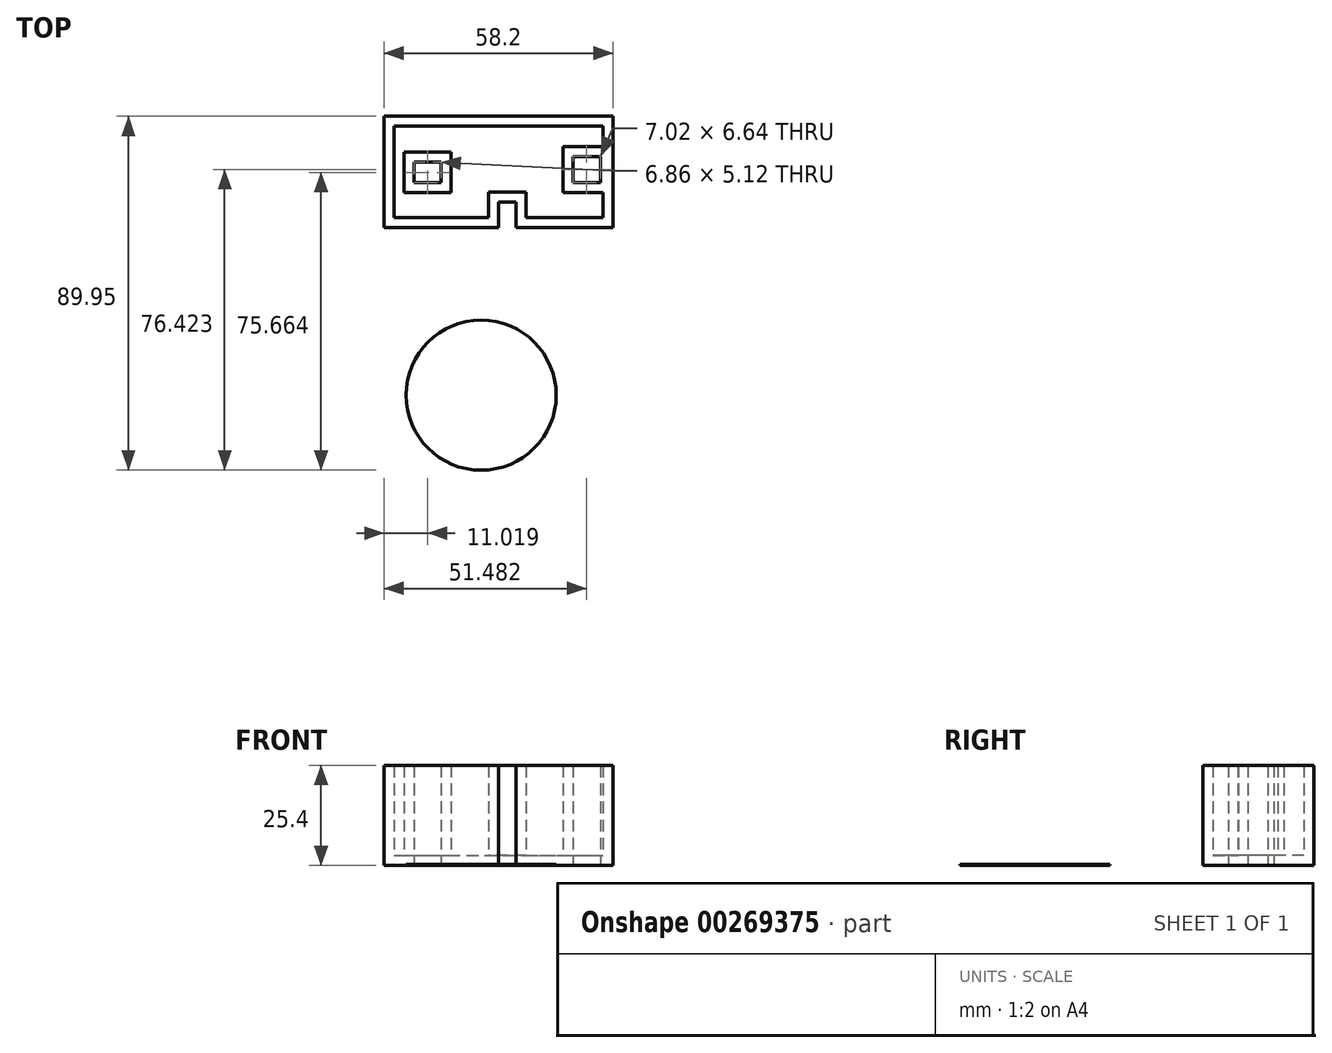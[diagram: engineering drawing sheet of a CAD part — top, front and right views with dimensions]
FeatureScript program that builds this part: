
annotation { "Feature Type Name" : "Feature", "Feature Type Description" : "" }
export const myFeature = defineFeature(function(context is Context, id is Id, definition is map)
    precondition{}
    {
        {
            var Q0;
            Q0=qCreatedBy(makeId("Top.planeOp"),FACE);
            var sketch = newSketch(context, id + "F0", { "sketchPlane" : qUnion([Q0])});
            skLineSegment(sketch, "E0.bottom", {"start": v(11.18, 38.08) * mm, "end": v(69.38, 38.08) * mm});
            skLineSegment(sketch, "E0.top", {"start": v(11.18, 9.83) * mm, "end": v(40.28, 9.83) * mm});
            skLineSegment(sketch, "E0.left", {"start": v(11.18, 38.08) * mm, "end": v(11.18, 9.83) * mm});
            skLineSegment(sketch, "E0.right", {"start": v(69.38, 38.08) * mm, "end": v(69.38, 9.83) * mm});
            skPoint(sketch, "E1.oppositeSnap0", {"position": v(40.28, 9.83) * mm});
            skLineSegment(sketch, "E1.top", {"start": v(44.73, 16.27) * mm, "end": v(40.28, 16.27) * mm});
            skLineSegment(sketch, "E1.left", {"start": v(44.73, 9.83) * mm, "end": v(44.73, 16.27) * mm});
            skLineSegment(sketch, "E1.right", {"start": v(40.28, 9.83) * mm, "end": v(40.28, 16.27) * mm});
            skLineSegment(sketch, "E2.trimOffspring", {"start": v(44.73, 9.83) * mm, "end": v(69.38, 9.83) * mm});
            skLineSegment(sketch, "E3.1", {"start": v(69.38, 38.08) * mm, "end": v(40, 69.4) * mm});
            skLineSegment(sketch, "E3.2", {"start": v(40, 69.4) * mm, "end": v(11.18, 38.08) * mm});
            skText(sketch, "E4", { "text": "SoMy", "fontName": "AllertaStencil-Regular.ttf"});
            skLineSegment(sketch, "E5.bottom", {"start": v(-62, 37.35) * mm, "end": v(-14.22, 37.35) * mm});
            skLineSegment(sketch, "E5.top", {"start": v(-62, 20.48) * mm, "end": v(-14.22, 20.48) * mm});
            skLineSegment(sketch, "E5.left", {"start": v(-62, 37.35) * mm, "end": v(-62, 20.48) * mm});
            skLineSegment(sketch, "E5.right", {"start": v(-14.22, 37.35) * mm, "end": v(-14.22, 20.48) * mm});
            skCircle(sketch, "E6", {"center": v(-37.4, 29.2) * mm, "radius": 9.47 * mm});
            skCircle(sketch, "E7", {"center": v(35.83, -32.8) * mm, "radius": 19.07 * mm});
            skCircle(sketch, "E8", {"center": v(35.83, -32.8) * mm, "radius": 9.53 * mm});
            skCircle(sketch, "E9", {"center": v(35.83, -32.8) * mm, "radius": 14.21 * mm});
            skCircle(sketch, "E10", {"center": v(-44.56, -17.44) * mm, "radius": 10.06 * mm});
            skLineSegment(sketch, "E11.bottom", {"start": v(59.15, 27.87) * mm, "end": v(66.17, 27.87) * mm});
            skLineSegment(sketch, "E11.top", {"start": v(59.15, 21.23) * mm, "end": v(66.17, 21.23) * mm});
            skLineSegment(sketch, "E11.left", {"start": v(59.15, 27.87) * mm, "end": v(59.15, 21.23) * mm});
            skLineSegment(sketch, "E11.right", {"start": v(66.17, 27.87) * mm, "end": v(66.17, 21.23) * mm});
            skLineSegment(sketch, "E12.bottom", {"start": v(18.77, 26.35) * mm, "end": v(25.63, 26.35) * mm});
            skLineSegment(sketch, "E12.top", {"start": v(18.77, 21.23) * mm, "end": v(25.63, 21.23) * mm});
            skLineSegment(sketch, "E12.left", {"start": v(18.77, 26.35) * mm, "end": v(18.77, 21.23) * mm});
            skLineSegment(sketch, "E12.right", {"start": v(25.63, 26.35) * mm, "end": v(25.63, 21.23) * mm});
            const initialGuessF0  = {"E4": [-0.06295, -0.06086, 1, 0, 0.01332]};
            skSetInitialGuess(sketch, initialGuessF0);
            skSolve(sketch);
        }
        {
            var Q0;
            Q0=sQuery(id+"F0.wireOp",EDGE,"E7");
            extrude(context, id + "F1", {"bodyType" : ToolBodyType.SURFACE, "surfaceEntities" : qUnion([Q0]), "oppositeDirection" : true, "depth" : 127.76 * mm});
        }
        {
            var Q0;
            Q0=sQuery(id+"F0.wireOp",EDGE,"E9");
            extrude(context, id + "F2", {"bodyType" : ToolBodyType.SURFACE, "surfaceEntities" : qUnion([Q0]), "depth" : 4.57 * mm});
        }
        {
            var Q0;
            Q0=sQuery(id+"F0.wireOp",EDGE,"E8");
            extrude(context, id + "F3", {"bodyType" : ToolBodyType.SURFACE, "surfaceEntities" : qUnion([Q0]), "depth" : 9.14 * mm});
        }
        {
            var Q0;
            Q0=makeQuery(id+"F0.imprint","IMPRINT",FACE,{"disambiguationData":[TD([[makeQuery(id+"F0.imprint","IMPRINT",EDGE,{"derivedFrom":sQuery(id+"F0.wireOp",EDGE,"E7")}),1.0]])]});
            var Q1;
            Q1=makeQuery(id+"F0.imprint","IMPRINT",FACE,{"disambiguationData":[TD([[makeQuery(id+"F0.imprint","IMPRINT",EDGE,{"derivedFrom":sQuery(id+"F0.wireOp",EDGE,"E8")}),-1.0]])]});
            var Q2;
            Q2=makeQuery(id+"F0.imprint","IMPRINT",FACE,{"disambiguationData":[TD([[makeQuery(id+"F0.imprint","IMPRINT",EDGE,{"derivedFrom":sQuery(id+"F0.wireOp",EDGE,"E8")}),1.0]])]});
            extrude(context, id + "F4", {"entities" : qUnion([Q0, Q1, Q2]), "depth" : 0.25 * mm});
        }
        {
            var Q0;
            Q0=makeQuery(id+"F0.imprint","IMPRINT",FACE,{"disambiguationData":[TD([[makeQuery(id+"F0.imprint","IMPRINT",EDGE,{"derivedFrom":sQuery(id+"F0.wireOp",EDGE,"E0.bottom")}),1.0]])]});
            var Q1;
            Q1=makeQuery(id+"F0.imprint","IMPRINT",FACE,{"disambiguationData":[TD([[makeQuery(id+"F0.imprint","IMPRINT",EDGE,{"derivedFrom":sQuery(id+"F0.wireOp",EDGE,"E0.top")}),1.0]])]});
            extrude(context, id + "F5", {"entities" : qUnion([Q0, Q1]), "depth" : 25.4 * mm});
        }
        {
            var Q0;
            Q0=makeQuery(id+"F2.opExtrude","SWEPT_BODY",BODY,{"disambiguationData":[OSD([sQuery(id+"F0.wireOp",EDGE,"E9")])]});
            var Q1;
            Q1=makeQuery(id+"F3.opExtrude","SWEPT_BODY",BODY,{"disambiguationData":[OSD([sQuery(id+"F0.wireOp",EDGE,"E8")])]});
            transform(context, id + "F6", {"entities" : qUnion([Q0, Q1]), "transformType" : TransformType.TRANSLATION_3D, "dx" : 0 * mm, "dy" : 0 * mm, "dz" : 0 * mm, "makeCopy" : false});
        }
        {
            var Q0;
            Q0=makeQuery(id+"F5.opExtrude","CAP_FACE",FACE,{"disambiguationData":[OSD([sQuery(id+"F0.wireOp",EDGE,"E0.top"),sQuery(id+"F0.wireOp",EDGE,"E0.left"),sQuery(id+"F0.wireOp",EDGE,"E0.right"),sQuery(id+"F0.wireOp",EDGE,"E1.top"),sQuery(id+"F0.wireOp",EDGE,"E1.left"),sQuery(id+"F0.wireOp",EDGE,"E1.right"),sQuery(id+"F0.wireOp",EDGE,"E2.trimOffspring"),sQuery(id+"F0.wireOp",EDGE,"E3.1"),sQuery(id+"F0.wireOp",EDGE,"E3.2"),sQuery(id+"F0.wireOp",EDGE,"E11.bottom"),sQuery(id+"F0.wireOp",EDGE,"E11.top"),sQuery(id+"F0.wireOp",EDGE,"E11.left"),sQuery(id+"F0.wireOp",EDGE,"E11.right"),sQuery(id+"F0.wireOp",EDGE,"E12.bottom"),sQuery(id+"F0.wireOp",EDGE,"E12.top"),sQuery(id+"F0.wireOp",EDGE,"E12.left"),sQuery(id+"F0.wireOp",EDGE,"E12.right")])],"isStart":false});
            shell(context, id + "F7", {"entities" : qUnion([Q0]), "thickness" : 2.54 * mm});
        }
    });
